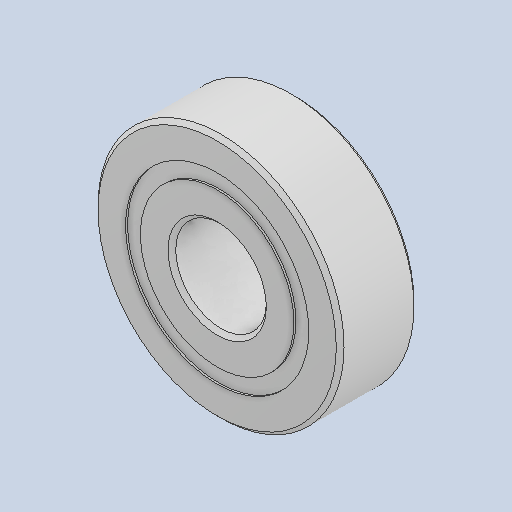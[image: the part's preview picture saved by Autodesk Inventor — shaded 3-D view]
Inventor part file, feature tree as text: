
AUTODESK INVENTOR PART (.ipt)
format: ipt  version: 2022 (Build 260153000, 153)  size: 563,712 bytes
history: mixed  units: mm
features: other x11, revolve x2, imported_body x1
ambient origin geometry x8: Origin, YZ Plane, XZ Plane, XY Plane, X Axis, Y Axis, Z Axis, Center Point
bodies: Solid1 (imported_parasolid), Solid2 (imported_parasolid), Solid3 (imported_parasolid), Solid4 (imported_parasolid), Solid5 (imported_parasolid), Solid6 (imported_parasolid), Solid7 (imported_parasolid), Solid8 (imported_parasolid), Solid9 (imported_parasolid), Solid10 (imported_parasolid), Solid11 (imported_parasolid), Solid12 (imported_parasolid), Solid13 (imported_parasolid)
feature tree (14):
  revolve  "Revolve2"  [1 undecoded]
  other  "CirPattern1[1]"
  other  "CirPattern1[2]"
  other  "CirPattern1[3]"
  other  "CirPattern1[4]"
  other  "CirPattern1[5]"
  other  "CirPattern1[6]"
  other  "CirPattern1[7]"
  other  "CirPattern1[8]"
  other  "CirPattern1[9]"
  other  "CirPattern1[10]"
  other  "CirPattern1[11]"
  revolve  "Revolve3"  [1 undecoded]
  imported_body  NMx_Import_Brep_tag  [imported B-rep: ~36 faces, bbox_mm=[16.571429, 0.0, 6.0]]
note: 2 required parameter values undecoded (feature->parameter linkage not recoverable at this tier; creation-order binding heuristic only, values carry confidence <= 0.55)
